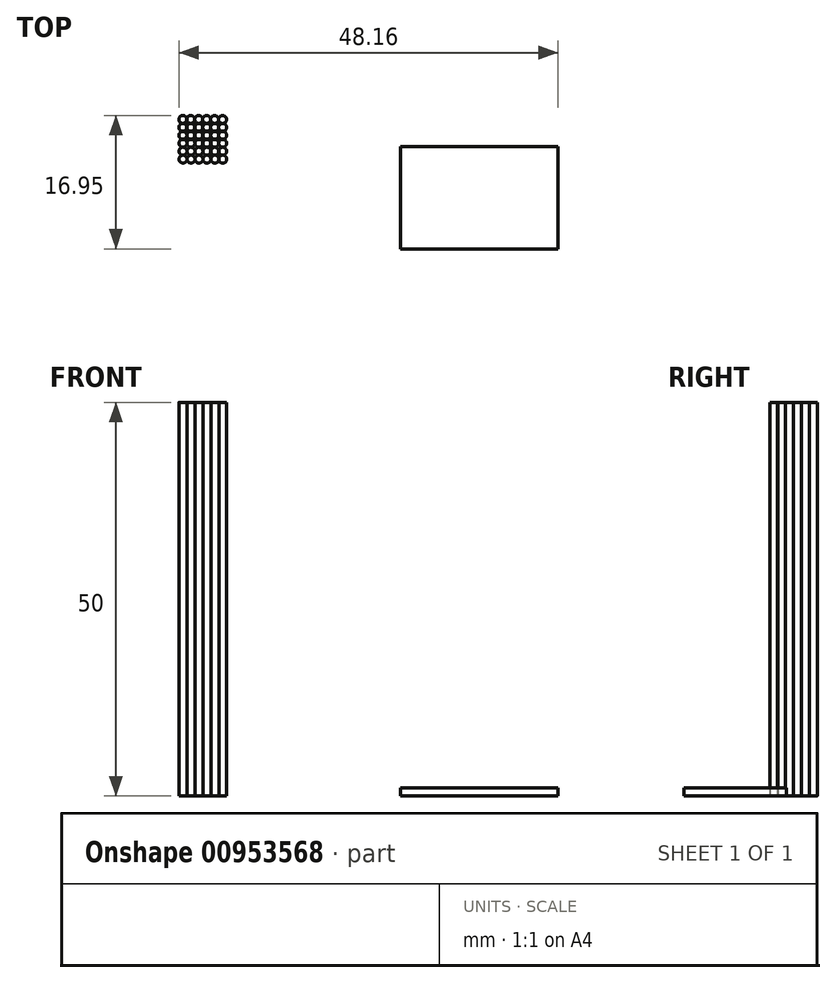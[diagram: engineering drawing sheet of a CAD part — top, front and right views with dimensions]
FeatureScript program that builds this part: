
annotation { "Feature Type Name" : "Feature", "Feature Type Description" : "" }
export const myFeature = defineFeature(function(context is Context, id is Id, definition is map)
    precondition{}
    {
        {
            var Q0;
            Q0=qCreatedBy(makeId("Top.planeOp"),FACE);
            var sketch = newSketch(context, id + "F0", { "sketchPlane" : qUnion([Q0])});
            skCircle(sketch, "E0", {"center": v(-24.18, 18.82) * mm, "radius": 0.5 * mm});
            skCircle(sketch, "E1.1.0.0", {"center": v(-23.17, 18.82) * mm, "radius": 0.5 * mm});
            skCircle(sketch, "E1.2.0.0", {"center": v(-22.16, 18.82) * mm, "radius": 0.5 * mm});
            skLineSegment(sketch, "E1.direction1", {"start": v(-24.18, 18.82) * mm, "end": v(-23.17, 18.82) * mm, "construction": true});
            skCircle(sketch, "E2.0.3.0", {"center": v(-21.15, 18.82) * mm, "radius": 0.5 * mm});
            skCircle(sketch, "E2.0.4.0", {"center": v(-20.14, 18.82) * mm, "radius": 0.5 * mm});
            skCircle(sketch, "E2.0.5.0", {"center": v(-19.13, 18.82) * mm, "radius": 0.5 * mm});
            skCircle(sketch, "E3.1.0.0", {"center": v(-20.13, 17.81) * mm, "radius": 0.5 * mm});
            skCircle(sketch, "E3.1.0.1", {"center": v(-24.17, 17.81) * mm, "radius": 0.5 * mm});
            skCircle(sketch, "E3.1.0.2", {"center": v(-22.15, 17.81) * mm, "radius": 0.5 * mm});
            skCircle(sketch, "E3.1.0.3", {"center": v(-21.14, 17.81) * mm, "radius": 0.5 * mm});
            skCircle(sketch, "E3.1.0.4", {"center": v(-19.12, 17.81) * mm, "radius": 0.5 * mm});
            skCircle(sketch, "E3.1.0.5", {"center": v(-23.16, 17.81) * mm, "radius": 0.5 * mm});
            skLineSegment(sketch, "E3.1.0.6", {"start": v(-24.17, 17.81) * mm, "end": v(-23.16, 17.81) * mm, "construction": true});
            skCircle(sketch, "E3.2.0.0", {"center": v(-20.13, 16.8) * mm, "radius": 0.5 * mm});
            skCircle(sketch, "E3.2.0.1", {"center": v(-24.17, 16.8) * mm, "radius": 0.5 * mm});
            skCircle(sketch, "E3.2.0.2", {"center": v(-22.15, 16.8) * mm, "radius": 0.5 * mm});
            skCircle(sketch, "E3.2.0.3", {"center": v(-21.14, 16.8) * mm, "radius": 0.5 * mm});
            skCircle(sketch, "E3.2.0.4", {"center": v(-19.12, 16.8) * mm, "radius": 0.5 * mm});
            skCircle(sketch, "E3.2.0.5", {"center": v(-23.16, 16.8) * mm, "radius": 0.5 * mm});
            skLineSegment(sketch, "E3.2.0.6", {"start": v(-24.17, 16.8) * mm, "end": v(-23.16, 16.8) * mm, "construction": true});
            skCircle(sketch, "E3.3.0.0", {"center": v(-20.12, 15.8) * mm, "radius": 0.5 * mm});
            skCircle(sketch, "E3.3.0.1", {"center": v(-24.16, 15.8) * mm, "radius": 0.5 * mm});
            skCircle(sketch, "E3.3.0.2", {"center": v(-22.14, 15.8) * mm, "radius": 0.5 * mm});
            skCircle(sketch, "E3.3.0.3", {"center": v(-21.13, 15.8) * mm, "radius": 0.5 * mm});
            skCircle(sketch, "E3.3.0.4", {"center": v(-19.1, 15.8) * mm, "radius": 0.5 * mm});
            skCircle(sketch, "E3.3.0.5", {"center": v(-23.15, 15.8) * mm, "radius": 0.5 * mm});
            skLineSegment(sketch, "E3.3.0.6", {"start": v(-24.16, 15.8) * mm, "end": v(-23.15, 15.8) * mm, "construction": true});
            skCircle(sketch, "E3.4.0.0", {"center": v(-20.11, 14.78) * mm, "radius": 0.5 * mm});
            skCircle(sketch, "E3.4.0.1", {"center": v(-24.15, 14.78) * mm, "radius": 0.5 * mm});
            skCircle(sketch, "E3.4.0.2", {"center": v(-22.13, 14.78) * mm, "radius": 0.5 * mm});
            skCircle(sketch, "E3.4.0.3", {"center": v(-21.12, 14.78) * mm, "radius": 0.5 * mm});
            skCircle(sketch, "E3.4.0.4", {"center": v(-19.1, 14.78) * mm, "radius": 0.5 * mm});
            skCircle(sketch, "E3.4.0.5", {"center": v(-23.14, 14.78) * mm, "radius": 0.5 * mm});
            skLineSegment(sketch, "E3.4.0.6", {"start": v(-24.15, 14.78) * mm, "end": v(-23.14, 14.78) * mm, "construction": true});
            skCircle(sketch, "E3.5.0.0", {"center": v(-20.1, 13.77) * mm, "radius": 0.5 * mm});
            skCircle(sketch, "E3.5.0.1", {"center": v(-24.15, 13.77) * mm, "radius": 0.5 * mm});
            skCircle(sketch, "E3.5.0.2", {"center": v(-22.13, 13.77) * mm, "radius": 0.5 * mm});
            skCircle(sketch, "E3.5.0.3", {"center": v(-21.12, 13.77) * mm, "radius": 0.5 * mm});
            skCircle(sketch, "E3.5.0.4", {"center": v(-19.1, 13.77) * mm, "radius": 0.5 * mm});
            skCircle(sketch, "E3.5.0.5", {"center": v(-23.14, 13.77) * mm, "radius": 0.5 * mm});
            skLineSegment(sketch, "E3.5.0.6", {"start": v(-24.15, 13.77) * mm, "end": v(-23.14, 13.77) * mm, "construction": true});
            skLineSegment(sketch, "E3.direction1", {"start": v(-24.18, 18.82) * mm, "end": v(-24.17, 17.81) * mm, "construction": true});
            skCircle(sketch, "E4.0.5.0", {"center": v(-7.45, 18.5) * mm, "radius": 0.5 * mm});
            skLineSegment(sketch, "E5.bottom", {"start": v(3.48, 2.37) * mm, "end": v(23.48, 2.37) * mm});
            skLineSegment(sketch, "E5.top", {"start": v(3.48, 15.37) * mm, "end": v(23.48, 15.37) * mm});
            skLineSegment(sketch, "E5.left", {"start": v(3.48, 2.37) * mm, "end": v(3.48, 15.37) * mm});
            skLineSegment(sketch, "E5.right", {"start": v(23.48, 2.37) * mm, "end": v(23.48, 15.37) * mm});
            skSolve(sketch);
        }
        {
            var Q0;
            Q0=makeQuery(id+"F0.imprint","IMPRINT",FACE,{"disambiguationData":[TD([[makeQuery(id+"F0.imprint","IMPRINT",EDGE,{"derivedFrom":sQuery(id+"F0.wireOp",EDGE,"E2.0.3.0")}),1.0]])]});
            var Q1;
            Q1=makeQuery(id+"F0.imprint","IMPRINT",FACE,{"disambiguationData":[TD([[makeQuery(id+"F0.imprint","IMPRINT",EDGE,{"derivedFrom":sQuery(id+"F0.wireOp",EDGE,"E3.3.0.4")}),1.0]])]});
            var Q2;
            Q2=makeQuery(id+"F0.imprint","IMPRINT",FACE,{"disambiguationData":[TD([[makeQuery(id+"F0.imprint","IMPRINT",EDGE,{"derivedFrom":sQuery(id+"F0.wireOp",EDGE,"E3.5.0.4")}),1.0]])]});
            var Q3;
            Q3=makeQuery(id+"F0.imprint","IMPRINT",FACE,{"disambiguationData":[TD([[makeQuery(id+"F0.imprint","IMPRINT",EDGE,{"derivedFrom":sQuery(id+"F0.wireOp",EDGE,"E2.0.5.0")}),1.0]])]});
            var Q4;
            Q4=makeQuery(id+"F0.imprint","IMPRINT",FACE,{"disambiguationData":[TD([[makeQuery(id+"F0.imprint","IMPRINT",EDGE,{"derivedFrom":sQuery(id+"F0.wireOp",EDGE,"E3.1.0.4")}),1.0]])]});
            var Q5;
            Q5=makeQuery(id+"F0.imprint","IMPRINT",FACE,{"disambiguationData":[TD([[makeQuery(id+"F0.imprint","IMPRINT",EDGE,{"derivedFrom":sQuery(id+"F0.wireOp",EDGE,"E3.3.0.0")}),1.0]])]});
            var Q6;
            Q6=makeQuery(id+"F0.imprint","IMPRINT",FACE,{"disambiguationData":[TD([[makeQuery(id+"F0.imprint","IMPRINT",EDGE,{"derivedFrom":sQuery(id+"F0.wireOp",EDGE,"E3.4.0.4")}),1.0]])]});
            var Q7;
            Q7=makeQuery(id+"F0.imprint","IMPRINT",FACE,{"disambiguationData":[TD([[makeQuery(id+"F0.imprint","IMPRINT",EDGE,{"derivedFrom":sQuery(id+"F0.wireOp",EDGE,"E3.4.0.0")}),1.0]])]});
            var Q8;
            Q8=makeQuery(id+"F0.imprint","IMPRINT",FACE,{"disambiguationData":[TD([[makeQuery(id+"F0.imprint","IMPRINT",EDGE,{"derivedFrom":sQuery(id+"F0.wireOp",EDGE,"E2.0.4.0")}),1.0]])]});
            var Q9;
            Q9=makeQuery(id+"F0.imprint","IMPRINT",FACE,{"disambiguationData":[TD([[makeQuery(id+"F0.imprint","IMPRINT",EDGE,{"derivedFrom":sQuery(id+"F0.wireOp",EDGE,"E1.2.0.0")}),1.0]])]});
            var Q10;
            Q10=makeQuery(id+"F0.imprint","IMPRINT",FACE,{"disambiguationData":[TD([[makeQuery(id+"F0.imprint","IMPRINT",EDGE,{"derivedFrom":sQuery(id+"F0.wireOp",EDGE,"E3.5.0.1")}),1.0]])]});
            var Q11;
            Q11=makeQuery(id+"F0.imprint","IMPRINT",FACE,{"disambiguationData":[TD([[makeQuery(id+"F0.imprint","IMPRINT",EDGE,{"derivedFrom":sQuery(id+"F0.wireOp",EDGE,"E3.3.0.3")}),1.0]])]});
            var Q12;
            Q12=makeQuery(id+"F0.imprint","IMPRINT",FACE,{"disambiguationData":[TD([[makeQuery(id+"F0.imprint","IMPRINT",EDGE,{"derivedFrom":sQuery(id+"F0.wireOp",EDGE,"E3.5.0.3")}),1.0]])]});
            var Q13;
            Q13=makeQuery(id+"F0.imprint","IMPRINT",FACE,{"disambiguationData":[TD([[makeQuery(id+"F0.imprint","IMPRINT",EDGE,{"derivedFrom":sQuery(id+"F0.wireOp",EDGE,"E3.5.0.0")}),1.0]])]});
            var Q14;
            Q14=makeQuery(id+"F0.imprint","IMPRINT",FACE,{"disambiguationData":[TD([[makeQuery(id+"F0.imprint","IMPRINT",EDGE,{"derivedFrom":sQuery(id+"F0.wireOp",EDGE,"E3.5.0.5")}),1.0]])]});
            var Q15;
            Q15=makeQuery(id+"F0.imprint","IMPRINT",FACE,{"disambiguationData":[TD([[makeQuery(id+"F0.imprint","IMPRINT",EDGE,{"derivedFrom":sQuery(id+"F0.wireOp",EDGE,"E3.2.0.4")}),1.0]])]});
            var Q16;
            Q16=makeQuery(id+"F0.imprint","IMPRINT",FACE,{"disambiguationData":[TD([[makeQuery(id+"F0.imprint","IMPRINT",EDGE,{"derivedFrom":sQuery(id+"F0.wireOp",EDGE,"E3.5.0.2")}),1.0]])]});
            var Q17;
            Q17=makeQuery(id+"F0.imprint","IMPRINT",FACE,{"disambiguationData":[TD([[makeQuery(id+"F0.imprint","IMPRINT",EDGE,{"derivedFrom":sQuery(id+"F0.wireOp",EDGE,"E3.1.0.3")}),1.0]])]});
            var Q18;
            Q18=makeQuery(id+"F0.imprint","IMPRINT",FACE,{"disambiguationData":[TD([[makeQuery(id+"F0.imprint","IMPRINT",EDGE,{"derivedFrom":sQuery(id+"F0.wireOp",EDGE,"E3.1.0.0")}),1.0]])]});
            var Q19;
            Q19=makeQuery(id+"F0.imprint","IMPRINT",FACE,{"disambiguationData":[TD([[makeQuery(id+"F0.imprint","IMPRINT",EDGE,{"derivedFrom":sQuery(id+"F0.wireOp",EDGE,"E3.4.0.2")}),1.0]])]});
            var Q20;
            Q20=makeQuery(id+"F0.imprint","IMPRINT",FACE,{"disambiguationData":[TD([[makeQuery(id+"F0.imprint","IMPRINT",EDGE,{"derivedFrom":sQuery(id+"F0.wireOp",EDGE,"E3.2.0.0")}),1.0]])]});
            var Q21;
            Q21=makeQuery(id+"F0.imprint","IMPRINT",FACE,{"disambiguationData":[TD([[makeQuery(id+"F0.imprint","IMPRINT",EDGE,{"derivedFrom":sQuery(id+"F0.wireOp",EDGE,"E3.2.0.3")}),1.0]])]});
            var Q22;
            Q22=makeQuery(id+"F0.imprint","IMPRINT",FACE,{"disambiguationData":[TD([[makeQuery(id+"F0.imprint","IMPRINT",EDGE,{"derivedFrom":sQuery(id+"F0.wireOp",EDGE,"E3.4.0.3")}),1.0]])]});
            var Q23;
            Q23=makeQuery(id+"F0.imprint","IMPRINT",FACE,{"disambiguationData":[TD([[makeQuery(id+"F0.imprint","IMPRINT",EDGE,{"derivedFrom":sQuery(id+"F0.wireOp",EDGE,"E3.4.0.5")}),1.0]])]});
            var Q24;
            Q24=makeQuery(id+"F0.imprint","IMPRINT",FACE,{"disambiguationData":[TD([[makeQuery(id+"F0.imprint","IMPRINT",EDGE,{"derivedFrom":sQuery(id+"F0.wireOp",EDGE,"E3.2.0.1")}),1.0]])]});
            var Q25;
            Q25=makeQuery(id+"F0.imprint","IMPRINT",FACE,{"disambiguationData":[TD([[makeQuery(id+"F0.imprint","IMPRINT",EDGE,{"derivedFrom":sQuery(id+"F0.wireOp",EDGE,"E3.1.0.2")}),1.0]])]});
            var Q26;
            Q26=makeQuery(id+"F0.imprint","IMPRINT",FACE,{"disambiguationData":[TD([[makeQuery(id+"F0.imprint","IMPRINT",EDGE,{"derivedFrom":sQuery(id+"F0.wireOp",EDGE,"E0")}),1.0]])]});
            var Q27;
            Q27=makeQuery(id+"F0.imprint","IMPRINT",FACE,{"disambiguationData":[TD([[makeQuery(id+"F0.imprint","IMPRINT",EDGE,{"derivedFrom":sQuery(id+"F0.wireOp",EDGE,"E3.4.0.1")}),1.0]])]});
            var Q28;
            Q28=makeQuery(id+"F0.imprint","IMPRINT",FACE,{"disambiguationData":[TD([[makeQuery(id+"F0.imprint","IMPRINT",EDGE,{"derivedFrom":sQuery(id+"F0.wireOp",EDGE,"E1.1.0.0")}),1.0]])]});
            var Q29;
            Q29=makeQuery(id+"F0.imprint","IMPRINT",FACE,{"disambiguationData":[TD([[makeQuery(id+"F0.imprint","IMPRINT",EDGE,{"derivedFrom":sQuery(id+"F0.wireOp",EDGE,"E3.1.0.1")}),1.0]])]});
            var Q30;
            Q30=makeQuery(id+"F0.imprint","IMPRINT",FACE,{"disambiguationData":[TD([[makeQuery(id+"F0.imprint","IMPRINT",EDGE,{"derivedFrom":sQuery(id+"F0.wireOp",EDGE,"E3.3.0.1")}),1.0]])]});
            var Q31;
            Q31=makeQuery(id+"F0.imprint","IMPRINT",FACE,{"disambiguationData":[TD([[makeQuery(id+"F0.imprint","IMPRINT",EDGE,{"derivedFrom":sQuery(id+"F0.wireOp",EDGE,"E3.3.0.2")}),1.0]])]});
            var Q32;
            Q32=makeQuery(id+"F0.imprint","IMPRINT",FACE,{"disambiguationData":[TD([[makeQuery(id+"F0.imprint","IMPRINT",EDGE,{"derivedFrom":sQuery(id+"F0.wireOp",EDGE,"E3.2.0.2")}),1.0]])]});
            var Q33;
            Q33=makeQuery(id+"F0.imprint","IMPRINT",FACE,{"disambiguationData":[TD([[makeQuery(id+"F0.imprint","IMPRINT",EDGE,{"derivedFrom":sQuery(id+"F0.wireOp",EDGE,"E3.2.0.5")}),1.0]])]});
            var Q34;
            Q34=makeQuery(id+"F0.imprint","IMPRINT",FACE,{"disambiguationData":[TD([[makeQuery(id+"F0.imprint","IMPRINT",EDGE,{"derivedFrom":sQuery(id+"F0.wireOp",EDGE,"E3.3.0.5")}),1.0]])]});
            var Q35;
            Q35=makeQuery(id+"F0.imprint","IMPRINT",FACE,{"disambiguationData":[TD([[makeQuery(id+"F0.imprint","IMPRINT",EDGE,{"derivedFrom":sQuery(id+"F0.wireOp",EDGE,"E3.1.0.5")}),1.0]])]});
            extrude(context, id + "F1", {"entities" : qUnion([Q0, Q1, Q2, Q3, Q4, Q5, Q6, Q7, Q8, Q9, Q10, Q11, Q12, Q13, Q14, Q15, Q16, Q17, Q18, Q19, Q20, Q21, Q22, Q23, Q24, Q25, Q26, Q27, Q28, Q29, Q30, Q31, Q32, Q33, Q34, Q35]), "depth" : 50 * mm, "offsetDistance" : 25 * mm});
        }
        {
            var Q0;
            Q0=makeQuery(id+"F0.imprint","IMPRINT",FACE,{"disambiguationData":[TD([[makeQuery(id+"F0.imprint","IMPRINT",EDGE,{"derivedFrom":sQuery(id+"F0.wireOp",EDGE,"E5.bottom")}),1.0]])]});
            extrude(context, id + "F2", {"entities" : qUnion([Q0]), "depth" : 1 * mm, "offsetDistance" : 25 * mm});
        }
    });
